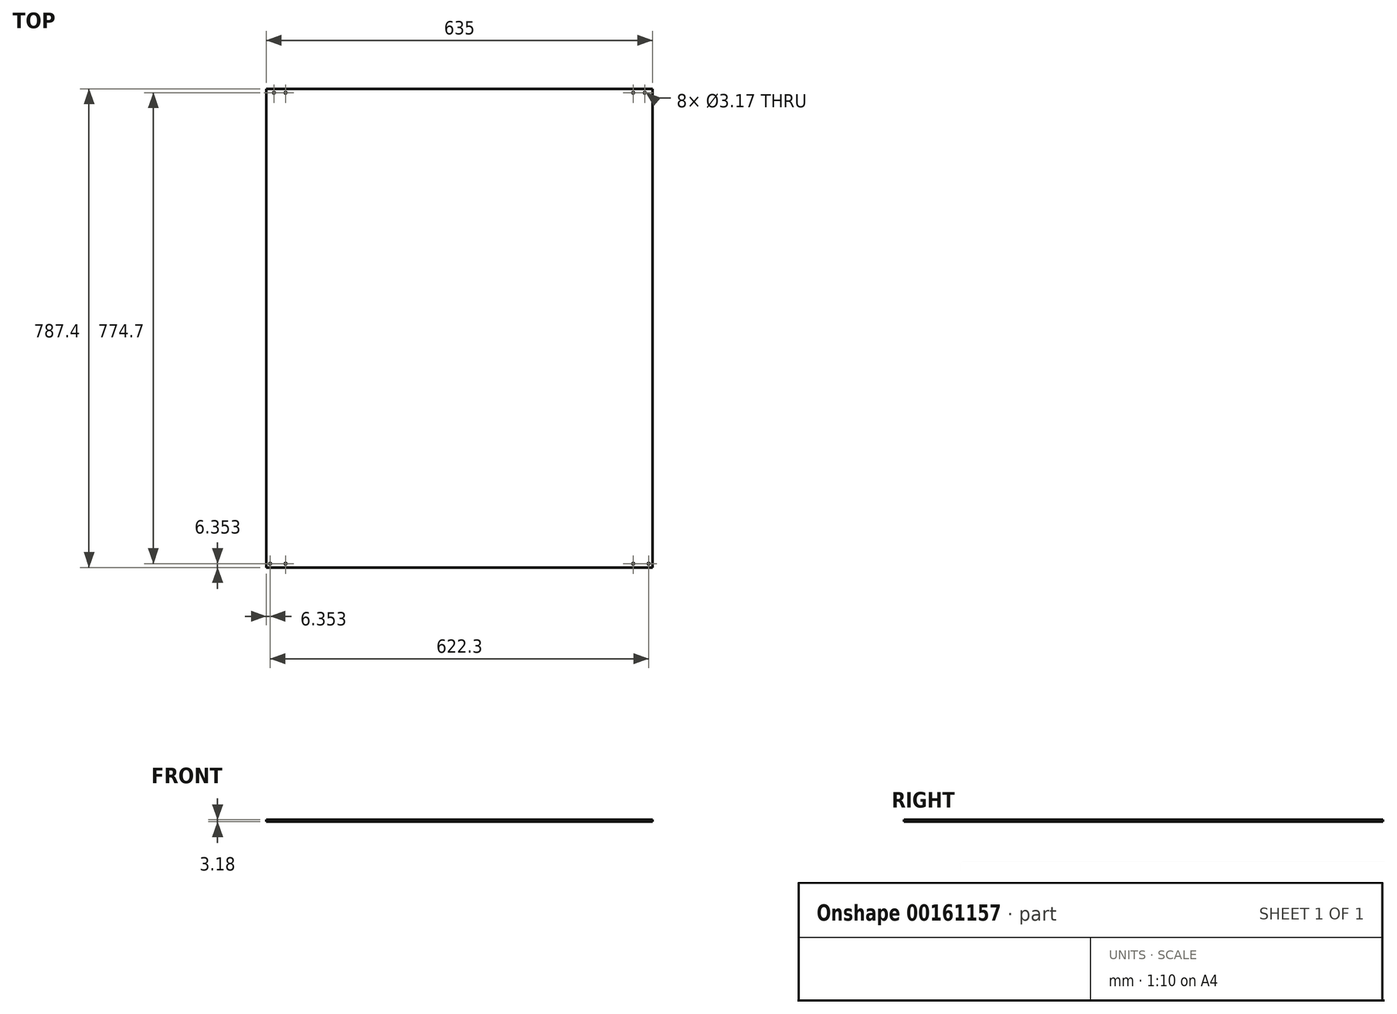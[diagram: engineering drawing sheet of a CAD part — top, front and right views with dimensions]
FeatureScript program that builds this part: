
annotation { "Feature Type Name" : "Feature", "Feature Type Description" : "" }
export const myFeature = defineFeature(function(context is Context, id is Id, definition is map)
    precondition{}
    {
        {
            var Q0;
            Q0=qCreatedBy(makeId("Top.planeOp"),FACE);
            var sketch = newSketch(context, id + "F0", { "sketchPlane" : qUnion([Q0])});
            skLineSegment(sketch, "E0", {"start": v(-336.4, 382.75) * mm, "end": v(298.6, 382.75) * mm});
            skLineSegment(sketch, "E1", {"start": v(298.6, 382.75) * mm, "end": v(298.6, -404.65) * mm});
            skLineSegment(sketch, "E2", {"start": v(298.6, -404.65) * mm, "end": v(-336.4, -404.65) * mm});
            skLineSegment(sketch, "E3", {"start": v(-336.4, -404.65) * mm, "end": v(-336.4, 382.75) * mm});
            skCircle(sketch, "E4", {"center": v(-330.06, -398.3) * mm, "radius": 1.59 * mm});
            skCircle(sketch, "E5", {"center": v(-304.66, -398.3) * mm, "radius": 1.59 * mm});
            skCircle(sketch, "E6", {"center": v(292.24, -398.3) * mm, "radius": 1.59 * mm});
            skCircle(sketch, "E7", {"center": v(266.84, -398.3) * mm, "radius": 1.59 * mm});
            skCircle(sketch, "E8", {"center": v(285.9, 376.4) * mm, "radius": 1.59 * mm});
            skCircle(sketch, "E9", {"center": v(266.84, 376.4) * mm, "radius": 1.59 * mm});
            skCircle(sketch, "E10", {"center": v(-323.7, 376.4) * mm, "radius": 1.59 * mm});
            skCircle(sketch, "E11", {"center": v(-304.66, 376.4) * mm, "radius": 1.59 * mm});
            skSolve(sketch);
        }
        {
            var Q0;
            Q0=makeQuery(id+"F0.imprint","IMPRINT",FACE,{"disambiguationData":[TD([[makeQuery(id+"F0.imprint","IMPRINT",EDGE,{"derivedFrom":sQuery(id+"F0.wireOp",EDGE,"E0")}),-1.0]])]});
            extrude(context, id + "F1", {"entities" : qUnion([Q0]), "oppositeDirection" : true, "depth" : 3.17 * mm});
        }
    });
